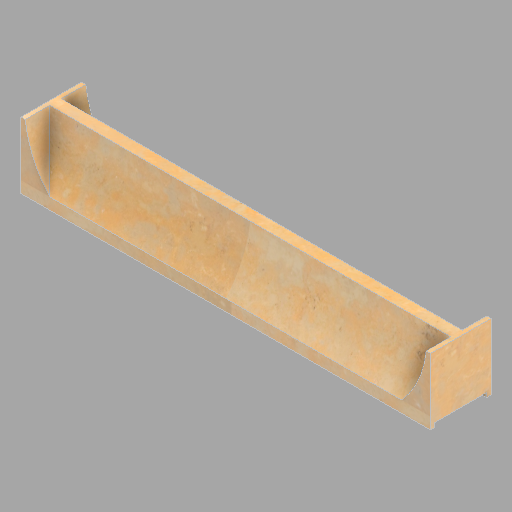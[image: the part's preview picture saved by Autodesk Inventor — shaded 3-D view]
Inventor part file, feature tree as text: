
AUTODESK INVENTOR PART (.ipt)
format: ipt  version: 2022.2 (Build 262287010, 287A)  size: 273,408 bytes
history: native  units: in
note: dims shown in document units (in); Inventor stores cm internally (conversion verified against a paired STEP export)
features: plane x1, extrude x1, sketch x1, other x1
ambient origin geometry x8: Origin, YZ Plane, XZ Plane, XY Plane, X Axis, Y Axis, Z Axis, Center Point
bodies: Solid1 (feature_tree)
feature tree (4):
  plane  "Work Plane1"
  extrude  "Extrusion1"  Depth=8.75in
  sketch  "Sketch1"  dims[d0=8.75in d1=8.75in d2=34.875in d3=0.0in]
  other  "North (6) (2) (1)"
